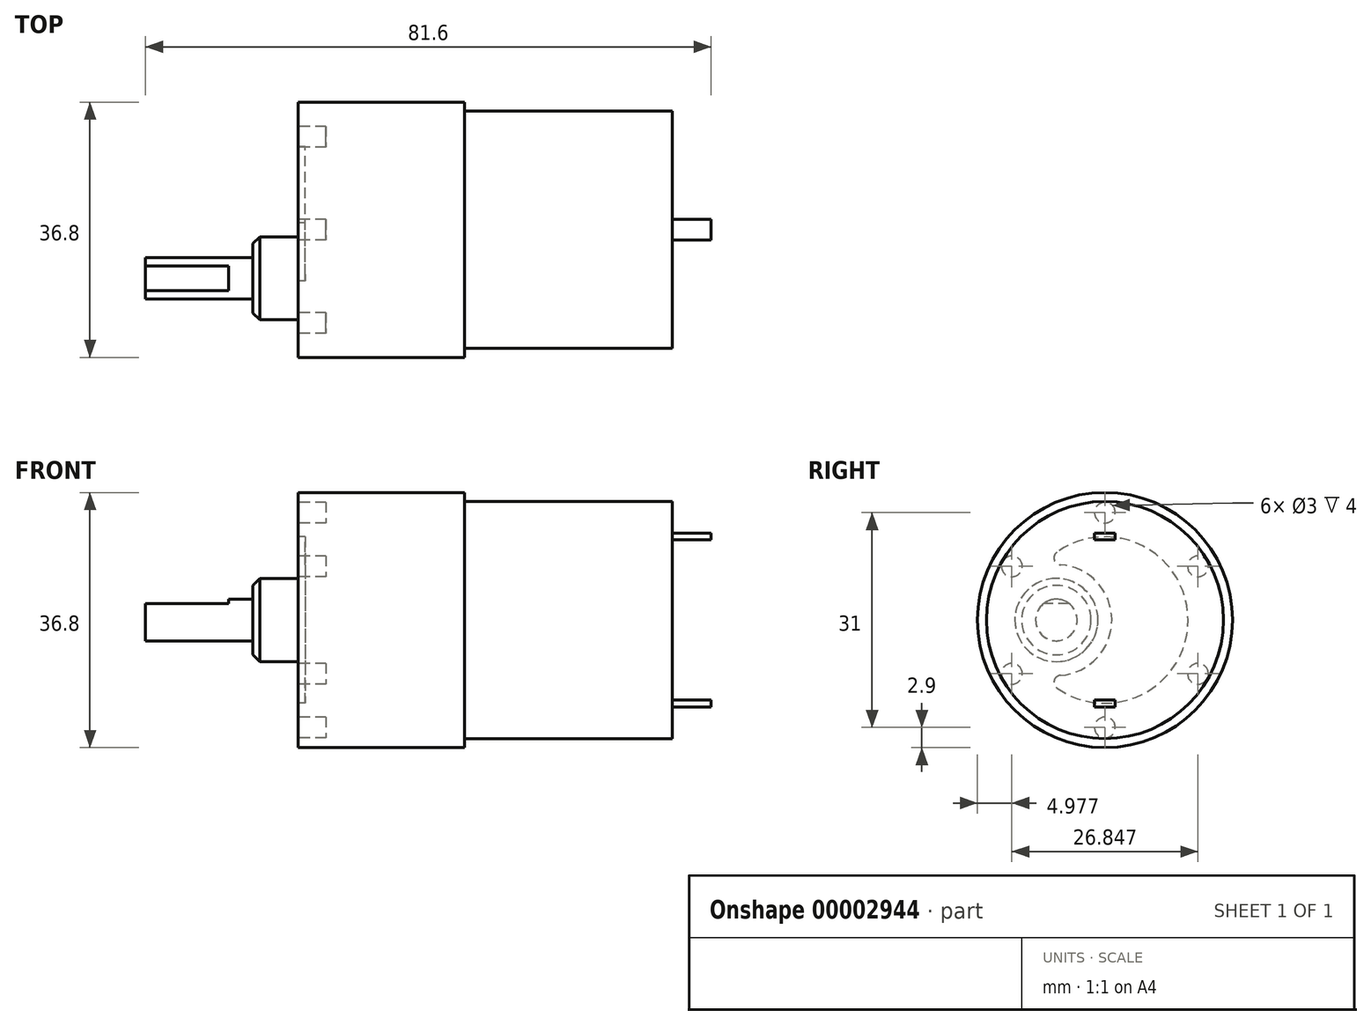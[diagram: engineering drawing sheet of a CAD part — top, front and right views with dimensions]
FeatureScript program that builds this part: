
annotation { "Feature Type Name" : "Feature", "Feature Type Description" : "" }
export const myFeature = defineFeature(function(context is Context, id is Id, definition is map)
    precondition{}
    {
        {
            var Q0;
            Q0=qCreatedBy(makeId("Front.planeOp"),FACE);
            var sketch = newSketch(context, id + "F0", { "sketchPlane" : qUnion([Q0])});
            skLineSegment(sketch, "E0", {"start": v(0, 0) * mm, "end": v(0, 18.4) * mm});
            skLineSegment(sketch, "E1", {"start": v(0, 18.4) * mm, "end": v(24, 18.4) * mm});
            skLineSegment(sketch, "E2", {"start": v(24, 18.4) * mm, "end": v(24, 17.1) * mm});
            skLineSegment(sketch, "E3", {"start": v(24, 17.1) * mm, "end": v(54, 17.1) * mm});
            skLineSegment(sketch, "E4", {"start": v(54, 17.1) * mm, "end": v(54, 0) * mm});
            skLineSegment(sketch, "E5", {"start": v(54, 0) * mm, "end": v(0, 0) * mm});
            skLineSegment(sketch, "E6.0.MirrorCS", {"start": v(24, -18.4) * mm, "end": v(24, -17.1) * mm, "construction": true});
            skLineSegment(sketch, "E6.1.MirrorCS", {"start": v(0, -18.4) * mm, "end": v(24, -18.4) * mm, "construction": true});
            skLineSegment(sketch, "E6.2.MirrorCS", {"start": v(54, -17.1) * mm, "end": v(54, 0) * mm, "construction": true});
            skLineSegment(sketch, "E6.3.MirrorCS", {"start": v(0, 0) * mm, "end": v(0, -18.4) * mm, "construction": true});
            skLineSegment(sketch, "E6.4.MirrorCS", {"start": v(24, -17.1) * mm, "end": v(54, -17.1) * mm, "construction": true});
            skSolve(sketch);
        }
        {
            var Q0;
            Q0=makeQuery(id+"F0.imprint","IMPRINT",FACE,{"disambiguationData":[TD([[makeQuery(id+"F0.imprint","IMPRINT",EDGE,{"derivedFrom":sQuery(id+"F0.wireOp",EDGE,"E0")}),-1.0]])]});
            var Q1;
            Q1=sQuery(id+"F0.wireOp",EDGE,"E5");
            revolve(context, id + "F1", {"entities" : qUnion([Q0]), "axis" : qUnion([Q1]), "revolveType" : RevolveType.FULL});
        }
        {
            var Q0;
            Q0=makeQuery(id+"F1.opRevolve","SWEPT_FACE",FACE,{"disambiguationData":[OSD([sQuery(id+"F0.wireOp",EDGE,"E0")])]});
            var sketch = newSketch(context, id + "F2", { "sketchPlane" : qUnion([Q0])});
            skCircle(sketch, "E7", {"center": v(0, 15.5) * mm, "radius": 1.5 * mm});
            skCircle(sketch, "E8.1.0", {"center": v(13.42, 7.75) * mm, "radius": 1.5 * mm});
            skCircle(sketch, "E8.2.0", {"center": v(13.42, -7.75) * mm, "radius": 1.5 * mm});
            skCircle(sketch, "E8.3.0", {"center": v(0, -15.5) * mm, "radius": 1.5 * mm});
            skCircle(sketch, "E8.4.0", {"center": v(-13.42, -7.75) * mm, "radius": 1.5 * mm});
            skCircle(sketch, "E8.5.0", {"center": v(-13.42, 7.75) * mm, "radius": 1.5 * mm});
            skPoint(sketch, "E8.center", {"position": v(0, 0) * mm});
            skLineSegment(sketch, "E8.anchor1", {"start": v(0, 0) * mm, "end": v(0, 15.5) * mm, "construction": true});
            skLineSegment(sketch, "E8.anchor2", {"start": v(0, 0) * mm, "end": v(-13.42, 7.75) * mm, "construction": true});
            skCircle(sketch, "E9", {"center": v(7, 0) * mm, "radius": 6 * mm});
            skCircle(sketch, "E10", {"center": v(7, 0) * mm, "radius": 3 * mm});
            skArc(sketch, "E11", {"start": v(6.94, 9.8) * mm, "mid": v(-12, 0) * mm, "end": v(6.94, -9.8) * mm});
            skArc(sketch, "E12", {"start": v(6.43, 7.98) * mm, "mid": v(-1, 0) * mm, "end": v(6.43, -7.98) * mm});
            skPoint(sketch, "E13.visualSharp", {"position": v(9.21, 7.69) * mm});
            skArc(sketch, "E13.filletArc", {"start": v(6.43, 7.98) * mm, "mid": v(7.32, 8.7) * mm, "end": v(6.94, 9.8) * mm});
            skPoint(sketch, "E14.visualSharp", {"position": v(9.21, -7.69) * mm});
            skArc(sketch, "E14.filletArc", {"start": v(6.94, -9.8) * mm, "mid": v(7.32, -8.7) * mm, "end": v(6.43, -7.98) * mm});
            skCircle(sketch, "E15", {"center": v(-15.5, 0) * mm, "radius": 1.5 * mm});
            skCircle(sketch, "E16.1.0", {"center": v(7.75, 13.42) * mm, "radius": 1.5 * mm});
            skCircle(sketch, "E16.2.0", {"center": v(7.75, -13.42) * mm, "radius": 1.5 * mm});
            skLineSegment(sketch, "E16.anchor1", {"start": v(0, 0) * mm, "end": v(-15.5, 0) * mm, "construction": true});
            skLineSegment(sketch, "E16.anchor2", {"start": v(0, 0) * mm, "end": v(7.75, -13.42) * mm, "construction": true});
            skSolve(sketch);
        }
        {
            var Q0;
            Q0=makeQuery(id+"F2.imprint","IMPRINT",FACE,{"disambiguationData":[TD([[makeQuery(id+"F2.imprint","IMPRINT",EDGE,{"derivedFrom":sQuery(id+"F2.wireOp",EDGE,"E11")}),1.0]])]});
            extrude(context, id + "F3", {"entities" : qUnion([Q0]), "operationType" : NewBodyOperationType.REMOVE, "oppositeDirection" : true, "depth" : 1 * mm});
        }
        {
            var Q0;
            Q0=makeQuery(id+"F2.imprint","IMPRINT",FACE,{"disambiguationData":[TD([[makeQuery(id+"F2.imprint","IMPRINT",EDGE,{"derivedFrom":sQuery(id+"F2.wireOp",EDGE,"E8.1.0")}),1.0]])]});
            var Q1;
            Q1=makeQuery(id+"F2.imprint","IMPRINT",FACE,{"disambiguationData":[TD([[makeQuery(id+"F2.imprint","IMPRINT",EDGE,{"derivedFrom":sQuery(id+"F2.wireOp",EDGE,"E8.2.0")}),1.0]])]});
            var Q2;
            Q2=makeQuery(id+"F2.imprint","IMPRINT",FACE,{"disambiguationData":[TD([[makeQuery(id+"F2.imprint","IMPRINT",EDGE,{"derivedFrom":sQuery(id+"F2.wireOp",EDGE,"E8.3.0")}),1.0]])]});
            var Q3;
            Q3=makeQuery(id+"F2.imprint","IMPRINT",FACE,{"disambiguationData":[TD([[makeQuery(id+"F2.imprint","IMPRINT",EDGE,{"derivedFrom":sQuery(id+"F2.wireOp",EDGE,"E8.4.0")}),1.0]])]});
            var Q4;
            Q4=makeQuery(id+"F2.imprint","IMPRINT",FACE,{"disambiguationData":[TD([[makeQuery(id+"F2.imprint","IMPRINT",EDGE,{"derivedFrom":sQuery(id+"F2.wireOp",EDGE,"E8.5.0")}),1.0]])]});
            var Q5;
            Q5=makeQuery(id+"F2.imprint","IMPRINT",FACE,{"disambiguationData":[TD([[makeQuery(id+"F2.imprint","IMPRINT",EDGE,{"derivedFrom":sQuery(id+"F2.wireOp",EDGE,"E7")}),1.0]])]});
            extrude(context, id + "F4", {"entities" : qUnion([Q0, Q1, Q2, Q3, Q4, Q5]), "operationType" : NewBodyOperationType.REMOVE, "oppositeDirection" : true, "depth" : 4 * mm});
        }
        {
            var Q0;
            Q0=makeQuery(id+"F2.imprint","IMPRINT",FACE,{"disambiguationData":[TD([[makeQuery(id+"F2.imprint","IMPRINT",EDGE,{"derivedFrom":sQuery(id+"F2.wireOp",EDGE,"E10")}),1.0]])]});
            extrude(context, id + "F5", {"entities" : qUnion([Q0]), "operationType" : NewBodyOperationType.ADD, "depth" : 22 * mm});
        }
        {
            var Q0;
            Q0=makeQuery(id+"F2.imprint","IMPRINT",FACE,{"disambiguationData":[TD([[makeQuery(id+"F2.imprint","IMPRINT",EDGE,{"derivedFrom":sQuery(id+"F2.wireOp",EDGE,"E9")}),1.0]])]});
            extrude(context, id + "F6", {"entities" : qUnion([Q0]), "operationType" : NewBodyOperationType.ADD, "depth" : 6.5 * mm});
        }
        {
            var Q0;
            Q0=makeQuery(id+"F6.opExtrude","CAP_EDGE",EDGE,{"disambiguationData":[OSD([sQuery(id+"F2.wireOp",EDGE,"E9")])],"isStart":false});
            chamfer(context, id + "F7", {"entities" : qUnion([Q0]), "width" : 1 * mm, "tangentPropagation" : true});
        }
        {
            var Q0;
            Q0=makeQuery(id+"F5.opExtrude","CAP_FACE",FACE,{"disambiguationData":[OSD([sQuery(id+"F2.wireOp",EDGE,"E10")])],"isStart":false});
            var sketch = newSketch(context, id + "F8", { "sketchPlane" : qUnion([Q0])});
            skCircle(sketch, "E17.0", {"center": v(7, 0) * mm, "radius": 3 * mm});
            skLineSegment(sketch, "E18", {"start": v(5.2, 2.4) * mm, "end": v(8.8, 2.4) * mm});
            skLineSegment(sketch, "E19", {"start": v(7, 2.4) * mm, "end": v(7, -3) * mm, "construction": true});
            skSolve(sketch);
        }
        {
            var Q0;
            {var subQ0=sQuery(id+"F8.wireOp",EDGE,"E18");Q0=makeQuery(id+"F8.imprint","IMPRINT",FACE,{"disambiguationData":[TD([[makeQuery(id+"F8.imprint","IMPRINT",EDGE,{"derivedFrom":subQ0}),1.0]])]});}
            extrude(context, id + "F9", {"entities" : qUnion([Q0]), "operationType" : NewBodyOperationType.REMOVE, "oppositeDirection" : true, "depth" : 12 * mm});
        }
        {
            var Q0;
            Q0=makeQuery(id+"F1.opRevolve","SWEPT_FACE",FACE,{"disambiguationData":[OSD([sQuery(id+"F0.wireOp",EDGE,"E4")])]});
            var sketch = newSketch(context, id + "F10", { "sketchPlane" : qUnion([Q0])});
            skLineSegment(sketch, "E20.rect.bottom", {"start": v(1.5, 11.55) * mm, "end": v(-1.5, 11.55) * mm});
            skLineSegment(sketch, "E20.rect.top", {"start": v(1.5, 12.55) * mm, "end": v(-1.5, 12.55) * mm});
            skLineSegment(sketch, "E20.rect.left", {"start": v(1.5, 11.55) * mm, "end": v(1.5, 12.55) * mm});
            skLineSegment(sketch, "E20.rect.right", {"start": v(-1.5, 11.55) * mm, "end": v(-1.5, 12.55) * mm});
            skPoint(sketch, "E20.rect.middle", {"position": v(0, 12.05) * mm});
            skLineSegment(sketch, "E21", {"start": v(-17.1, 0) * mm, "end": v(17.1, 0) * mm, "construction": true});
            skPoint(sketch, "E22.0.MirrorP", {"position": v(0, -12.05) * mm});
            skLineSegment(sketch, "E22.1.MirrorCS", {"start": v(-1.5, -11.55) * mm, "end": v(-1.5, -12.55) * mm});
            skLineSegment(sketch, "E22.2.MirrorCS", {"start": v(1.5, -12.55) * mm, "end": v(-1.5, -12.55) * mm});
            skLineSegment(sketch, "E22.3.MirrorCS", {"start": v(1.5, -11.55) * mm, "end": v(1.5, -12.55) * mm});
            skLineSegment(sketch, "E22.4.MirrorCS", {"start": v(1.5, -11.55) * mm, "end": v(-1.5, -11.55) * mm});
            skSolve(sketch);
        }
        {
            var Q0;
            Q0=makeQuery(id+"F10.imprint","IMPRINT",FACE,{"disambiguationData":[TD([[makeQuery(id+"F10.imprint","IMPRINT",EDGE,{"derivedFrom":sQuery(id+"F10.wireOp",EDGE,"E20.rect.bottom")}),-1.0]])]});
            var Q1;
            Q1=makeQuery(id+"F10.imprint","IMPRINT",FACE,{"disambiguationData":[TD([[makeQuery(id+"F10.imprint","IMPRINT",EDGE,{"derivedFrom":sQuery(id+"F10.wireOp",EDGE,"E22.1.MirrorCS")}),1.0]])]});
            extrude(context, id + "F11", {"entities" : qUnion([Q0, Q1]), "operationType" : NewBodyOperationType.ADD, "depth" : 5.6 * mm});
        }
    });
